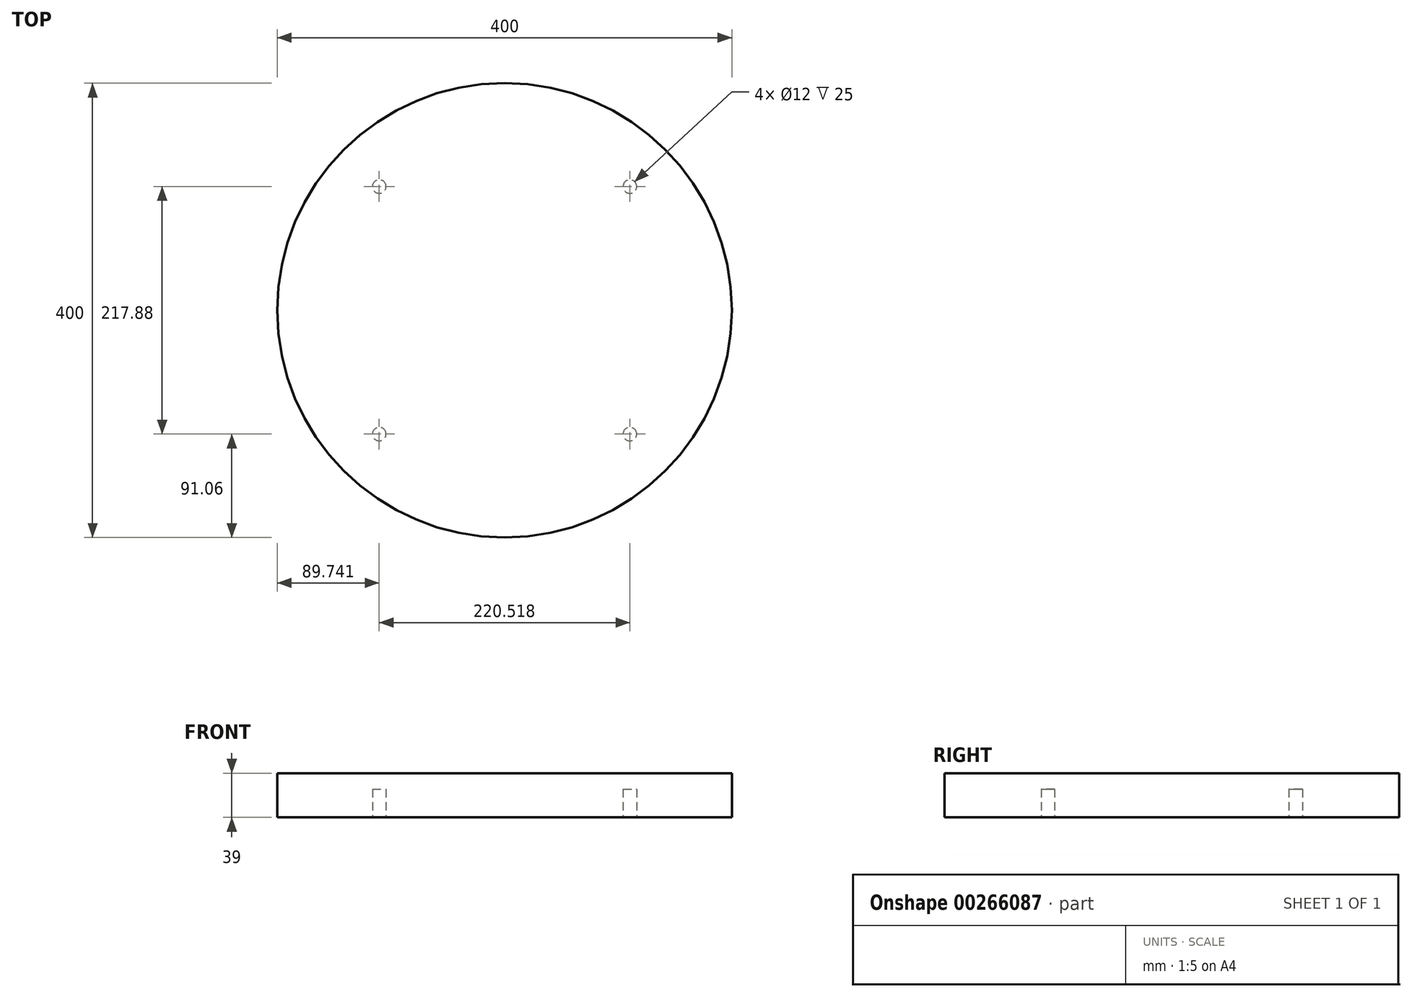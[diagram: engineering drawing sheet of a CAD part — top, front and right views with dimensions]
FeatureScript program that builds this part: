
annotation { "Feature Type Name" : "Feature", "Feature Type Description" : "" }
export const myFeature = defineFeature(function(context is Context, id is Id, definition is map)
    precondition{}
    {
        {
            var Q0;
            Q0=qCreatedBy(makeId("Top.planeOp"),FACE);
            var sketch = newSketch(context, id + "F0", { "sketchPlane" : qUnion([Q0])});
            skCircle(sketch, "E0", {"center": v(0, 0) * mm, "radius": 200 * mm});
            skSolve(sketch);
        }
        {
            var Q0;
            Q0 = qSketchRegion(id + "F0", true);
            extrude(context, id + "F1", {"entities" : qUnion([Q0]), "depth" : 39 * mm});
        }
        {
            var Q0;
            Q0=makeQuery(id+"F1.opExtrude","CAP_FACE",FACE,{"disambiguationData":[OSD([sQuery(id+"F0.wireOp",EDGE,"E0")])],"isStart":true});
            var sketch = newSketch(context, id + "F2", { "sketchPlane" : qUnion([Q0])});
            skLineSegment(sketch, "E1.bottom", {"start": v(-110.26, -108.94) * mm, "end": v(110.26, -108.94) * mm, "construction": true});
            skLineSegment(sketch, "E1.top", {"start": v(-110.26, 108.94) * mm, "end": v(110.26, 108.94) * mm, "construction": true});
            skLineSegment(sketch, "E1.left", {"start": v(-110.26, -108.94) * mm, "end": v(-110.26, 108.94) * mm, "construction": true});
            skLineSegment(sketch, "E1.right", {"start": v(110.26, -108.94) * mm, "end": v(110.26, 108.94) * mm, "construction": true});
            skPoint(sketch, "E1.middle", {"position": v(0, 0) * mm});
            skCircle(sketch, "E2", {"center": v(0, 0) * mm, "radius": 155 * mm, "construction": true});
            skCircle(sketch, "E3", {"center": v(110.26, 108.94) * mm, "radius": 20 * mm, "construction": true});
            skCircle(sketch, "E4", {"center": v(110.26, 108.94) * mm, "radius": 6 * mm});
            skCircle(sketch, "E5", {"center": v(110.26, -108.94) * mm, "radius": 6 * mm});
            skCircle(sketch, "E6", {"center": v(-110.26, -108.94) * mm, "radius": 6 * mm});
            skCircle(sketch, "E7", {"center": v(-110.26, 108.94) * mm, "radius": 6 * mm});
            skSolve(sketch);
        }
        {
            var Q0;
            Q0 = qSketchRegion(id + "F2", true);
            extrude(context, id + "F3", {"entities" : qUnion([Q0]), "operationType" : NewBodyOperationType.REMOVE, "oppositeDirection" : true, "depth" : 25 * mm});
        }
    });
